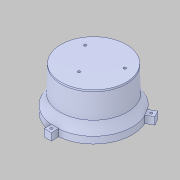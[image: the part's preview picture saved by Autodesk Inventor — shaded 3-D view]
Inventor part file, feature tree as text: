
AUTODESK INVENTOR PART (.ipt)
format: ipt  version: 2019 (Build 230136000, 136)  size: 577,024 bytes
history: native  units: in
note: dims shown in document units (in); Inventor stores cm internally (conversion verified against a paired STEP export)
features: sketch x4, extrude x2, plane x1, revolve x1, boolean_combine x1, delete_face x1, hole x1, pattern_circular x1, other x1
ambient origin geometry x8: Origin, YZ Plane, XZ Plane, XY Plane, X Axis, Y Axis, Z Axis, Center Point
bodies: Solid1 (feature_tree), Solid2 (feature_tree)
feature tree (13):
  plane  "Work Plane1"
  revolve  "Revolution1"  [1 undecoded]
  boolean_combine  "Combine1"
  delete_face  "Delete Face1"
  extrude  "Extrusion1"  Depth=0.5906in
  hole  "Hole1"  [1 undecoded]
  pattern_circular  "Circular Pattern1"  Count=3  [1 undecoded]
  extrude  "Extrusion2"  Depth=0.3937in TaperAngle=0.0deg
  sketch  "Sketch1"  dims[d0=0.0in d1=0.5906in]
  sketch  "Sketch2"  dims[d2=0.5906in d3=0.5906in]
  sketch  "Sketch3"  dims[d4=0.5906in d5=90.0deg]
  sketch  "Sketch5"  dims[d6=0.5906in d7=1.1811in d8=0.5906in d9=0.0in d10=0.1969in d11=0.2362in d12=0.1575in d13=0.0787in d14=90.0deg d15=0.315in d16=0.8108in d17=0.2953in d18=0.2953in d19=1.1811in d20=2.4737in d22=3.7402in d24=0.1969in d25=0.1969in d26=0.1969in d28=0.8246in d29=0.3937in d30=0.0in]
  other  "Scale1"
note: 3 required parameter values undecoded (feature->parameter linkage not recoverable at this tier; creation-order binding heuristic only, values carry confidence <= 0.55)